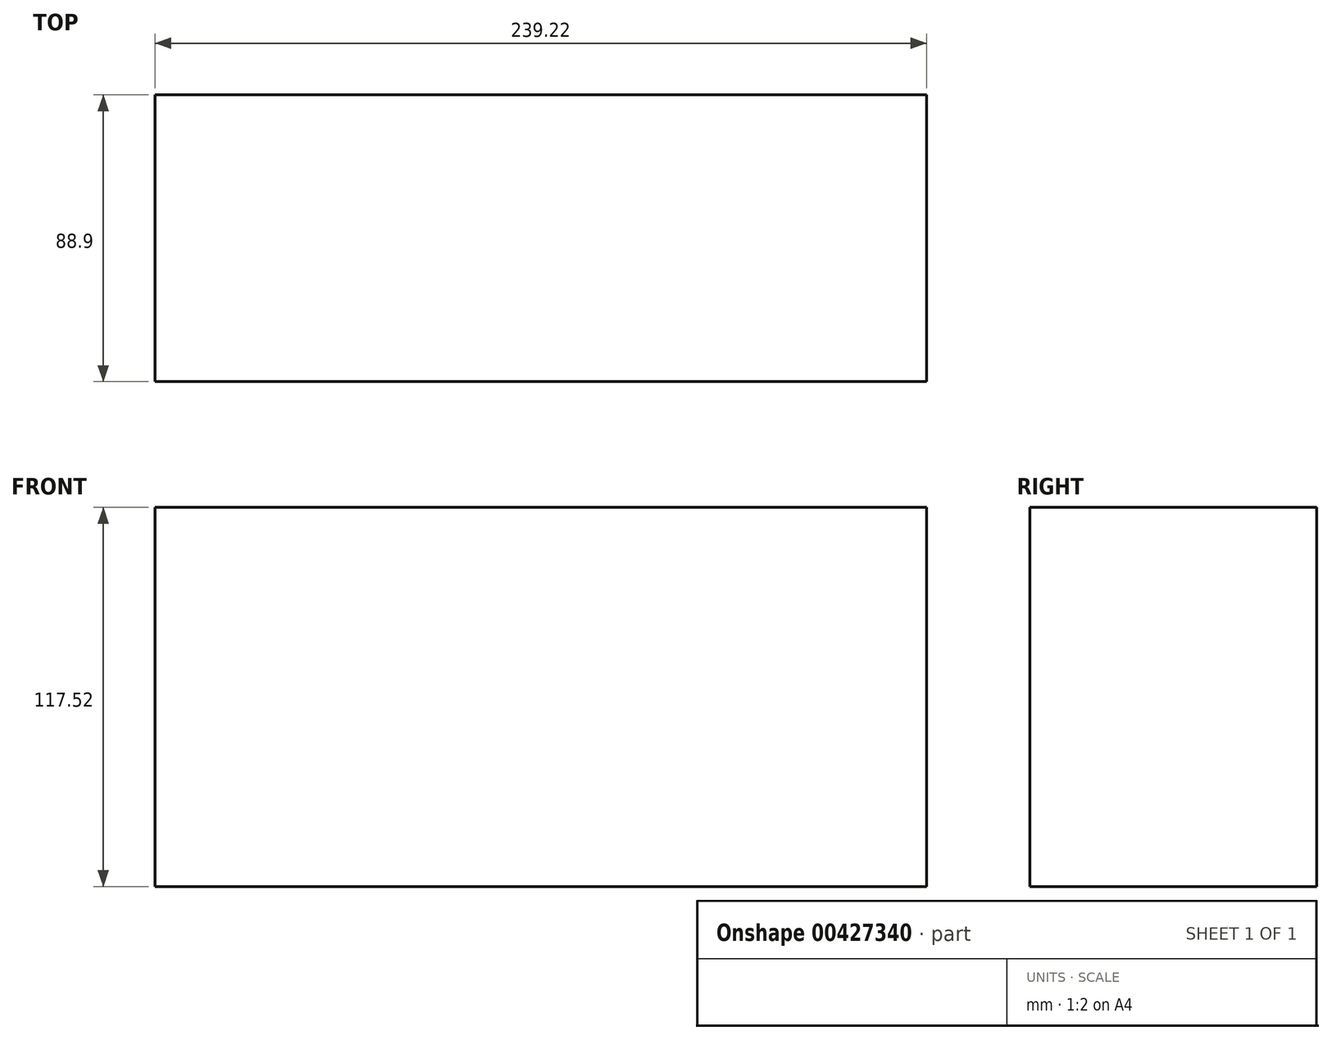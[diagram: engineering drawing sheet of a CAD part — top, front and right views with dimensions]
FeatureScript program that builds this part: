
annotation { "Feature Type Name" : "Feature", "Feature Type Description" : "" }
export const myFeature = defineFeature(function(context is Context, id is Id, definition is map)
    precondition{}
    {
        {
            var Q0;
            Q0=qCreatedBy(makeId("Front.planeOp"),FACE);
            var sketch = newSketch(context, id + "F0", { "sketchPlane" : qUnion([Q0])});
            skLineSegment(sketch, "E0.bottom", {"start": v(119.61, -58.76) * mm, "end": v(-119.61, -58.76) * mm});
            skLineSegment(sketch, "E0.top", {"start": v(119.61, 58.76) * mm, "end": v(-119.61, 58.76) * mm});
            skLineSegment(sketch, "E0.left", {"start": v(119.61, -58.76) * mm, "end": v(119.61, 58.76) * mm});
            skLineSegment(sketch, "E0.right", {"start": v(-119.61, -58.76) * mm, "end": v(-119.61, 58.76) * mm});
            skPoint(sketch, "E0.middle", {"position": v(0, 0) * mm});
            skSolve(sketch);
        }
        {
            var Q0;
            Q0=makeQuery(id+"F0.imprint","IMPRINT",FACE,{"disambiguationData":[TD([[makeQuery(id+"F0.imprint","IMPRINT",EDGE,{"derivedFrom":sQuery(id+"F0.wireOp",EDGE,"E0.bottom")}),-1.0]])]});
            extrude(context, id + "F1", {"entities" : qUnion([Q0]), "depth" : 88.9 * mm});
        }
    });
